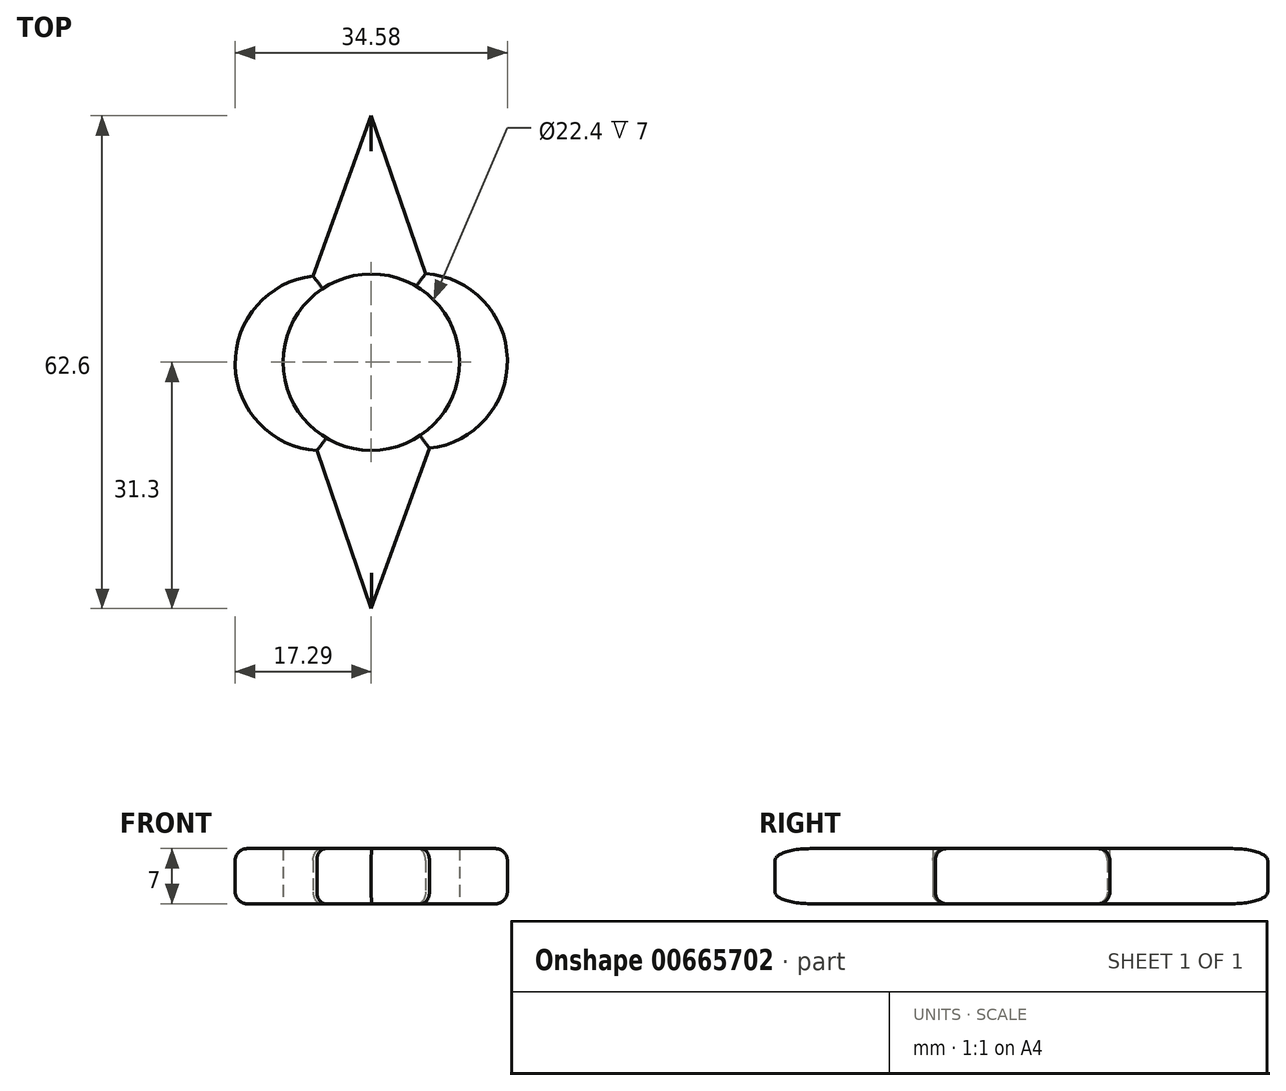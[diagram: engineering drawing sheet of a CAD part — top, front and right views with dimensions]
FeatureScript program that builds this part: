
annotation { "Feature Type Name" : "Feature", "Feature Type Description" : "" }
export const myFeature = defineFeature(function(context is Context, id is Id, definition is map)
    precondition{}
    {
        {
            var Q0;
            Q0=qCreatedBy(makeId("Top.planeOp"),FACE);
            var sketch = newSketch(context, id + "F0", { "sketchPlane" : qUnion([Q0])});
            skCircle(sketch, "E0", {"center": v(0, 0) * mm, "radius": 11.2 * mm});
            skLineSegment(sketch, "E1", {"start": v(-7.4, 10.94) * mm, "end": v(0, 31.3) * mm});
            skLineSegment(sketch, "E2", {"start": v(0, 31.3) * mm, "end": v(6.9, 11.25) * mm});
            skLineSegment(sketch, "E3.1.0", {"start": v(7.4, -10.94) * mm, "end": v(0, -31.3) * mm});
            skLineSegment(sketch, "E3.1.1", {"start": v(0, -31.3) * mm, "end": v(-6.9, -11.25) * mm});
            skArc(sketch, "E4", {"start": v(7.4, -10.94) * mm, "mid": v(17.28, 0.38) * mm, "end": v(6.9, 11.25) * mm});
            skArc(sketch, "E5.1.0", {"start": v(-7.4, 10.94) * mm, "mid": v(-17.28, -0.38) * mm, "end": v(-6.9, -11.25) * mm});
            skSolve(sketch);
        }
        {
            var Q0;
            Q0=makeQuery(id+"F0.imprint","IMPRINT",FACE,{"disambiguationData":[TD([[makeQuery(id+"F0.imprint","IMPRINT",EDGE,{"derivedFrom":sQuery(id+"F0.wireOp",EDGE,"E0")}),-1.0]])]});
            extrude(context, id + "F1", {"entities" : qUnion([Q0]), "depth" : 7 * mm, "offsetDistance" : 25 * mm});
        }
        {
            var Q0;
            Q0=makeQuery(id+"F1.opExtrude","CAP_EDGE",EDGE,{"disambiguationData":[OSD([sQuery(id+"F0.wireOp",EDGE,"E3.1.0")])],"isStart":false});
            var Q1;
            Q1=makeQuery(id+"F1.opExtrude","CAP_EDGE",EDGE,{"disambiguationData":[OSD([sQuery(id+"F0.wireOp",EDGE,"E3.1.1")])],"isStart":false});
            var Q2;
            Q2=makeQuery(id+"F1.opExtrude","CAP_EDGE",EDGE,{"disambiguationData":[OSD([sQuery(id+"F0.wireOp",EDGE,"E5.1.0")])],"isStart":false});
            var Q3;
            Q3=makeQuery(id+"F1.opExtrude","CAP_EDGE",EDGE,{"disambiguationData":[OSD([sQuery(id+"F0.wireOp",EDGE,"E1")])],"isStart":false});
            var Q4;
            Q4=makeQuery(id+"F1.opExtrude","CAP_EDGE",EDGE,{"disambiguationData":[OSD([sQuery(id+"F0.wireOp",EDGE,"E4")])],"isStart":false});
            var Q5;
            Q5=makeQuery(id+"F1.opExtrude","CAP_EDGE",EDGE,{"disambiguationData":[OSD([sQuery(id+"F0.wireOp",EDGE,"E2")])],"isStart":false});
            var Q6;
            Q6=makeQuery(id+"F1.opExtrude","CAP_EDGE",EDGE,{"disambiguationData":[OSD([sQuery(id+"F0.wireOp",EDGE,"E3.1.0")])],"isStart":true});
            var Q7;
            Q7=makeQuery(id+"F1.opExtrude","CAP_EDGE",EDGE,{"disambiguationData":[OSD([sQuery(id+"F0.wireOp",EDGE,"E4")])],"isStart":true});
            var Q8;
            Q8=makeQuery(id+"F1.opExtrude","CAP_EDGE",EDGE,{"disambiguationData":[OSD([sQuery(id+"F0.wireOp",EDGE,"E2")])],"isStart":true});
            var Q9;
            Q9=makeQuery(id+"F1.opExtrude","CAP_EDGE",EDGE,{"disambiguationData":[OSD([sQuery(id+"F0.wireOp",EDGE,"E1")])],"isStart":true});
            var Q10;
            Q10=makeQuery(id+"F1.opExtrude","CAP_EDGE",EDGE,{"disambiguationData":[OSD([sQuery(id+"F0.wireOp",EDGE,"E5.1.0")])],"isStart":true});
            var Q11;
            Q11=makeQuery(id+"F1.opExtrude","CAP_EDGE",EDGE,{"disambiguationData":[OSD([sQuery(id+"F0.wireOp",EDGE,"E3.1.1")])],"isStart":true});
            fillet(context, id + "F2", {"entities" : qUnion([Q0, Q1, Q2, Q3, Q4, Q5, Q6, Q7, Q8, Q9, Q10, Q11]), "radius" : 1.5 * mm, "tangentPropagation" : true, "allowEdgeOverflow" : false});
        }
    });
